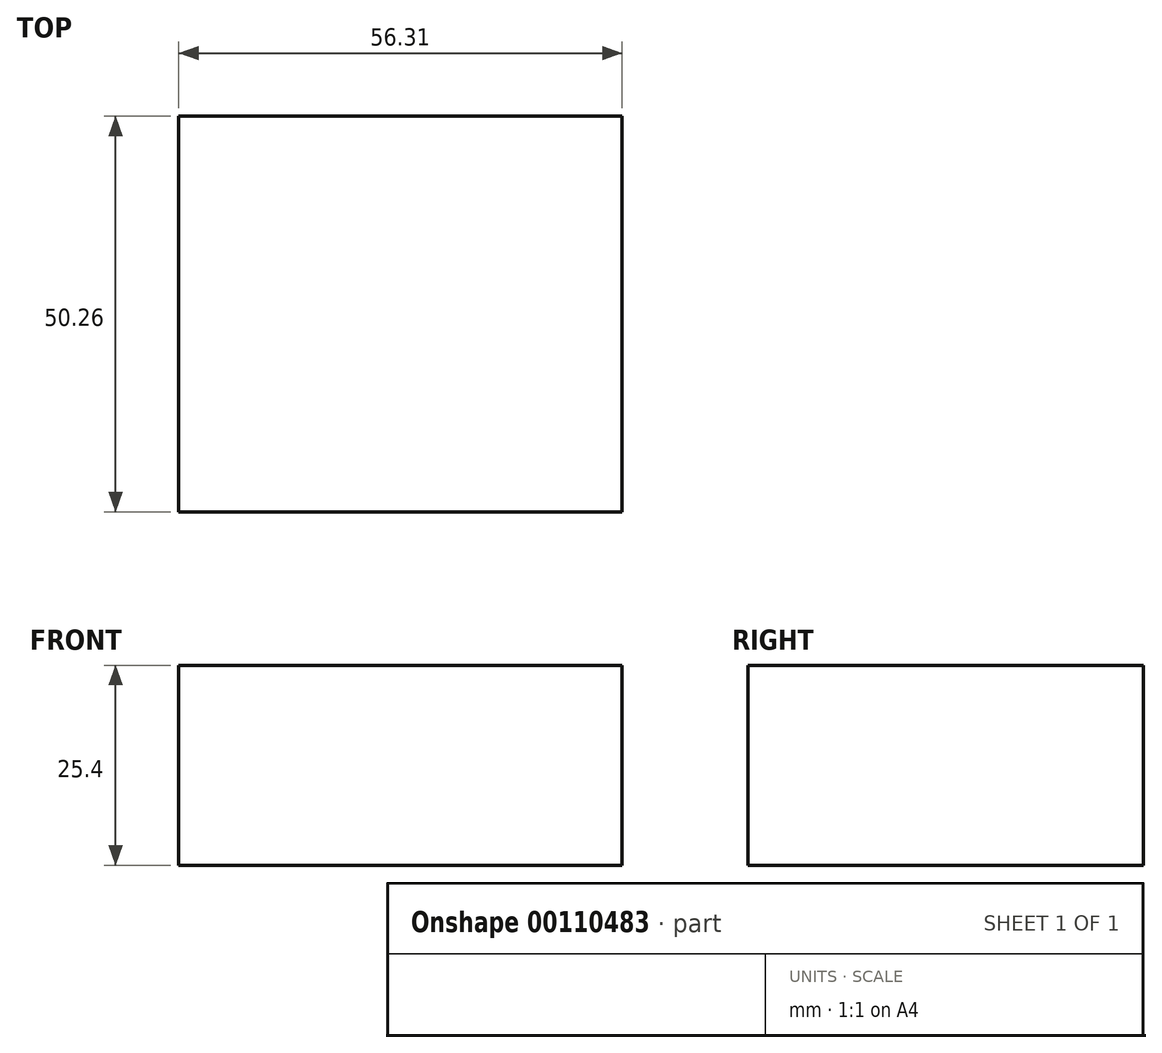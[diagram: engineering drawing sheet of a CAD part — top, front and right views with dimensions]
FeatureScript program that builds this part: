
annotation { "Feature Type Name" : "Feature", "Feature Type Description" : "" }
export const myFeature = defineFeature(function(context is Context, id is Id, definition is map)
    precondition{}
    {
        {
            var Q0;
            Q0=qCreatedBy(makeId("Top.planeOp"),FACE);
            var sketch = newSketch(context, id + "F1", { "sketchPlane" : qUnion([Q0])});
            skLineSegment(sketch, "E0.bottom", {"start": v(-21.65, 0) * mm, "end": v(34.66, 0) * mm});
            skLineSegment(sketch, "E0.top", {"start": v(-21.65, -50.26) * mm, "end": v(34.66, -50.26) * mm});
            skLineSegment(sketch, "E0.left", {"start": v(-21.65, 0) * mm, "end": v(-21.65, -50.26) * mm});
            skLineSegment(sketch, "E0.right", {"start": v(34.66, 0) * mm, "end": v(34.66, -50.26) * mm});
            skSolve(sketch);
        }
        {
            var Q0;
            Q0=makeQuery(id+"F1.imprint","IMPRINT",FACE,{"disambiguationData":[TD([[makeQuery(id+"F1.imprint","IMPRINT",EDGE,{"derivedFrom":sQuery(id+"F1.wireOp",EDGE,"E0.bottom")}),-1.0]])]});
            extrude(context, id + "F0", {"entities" : qUnion([Q0]), "depth" : 25.4 * mm});
        }
    });
